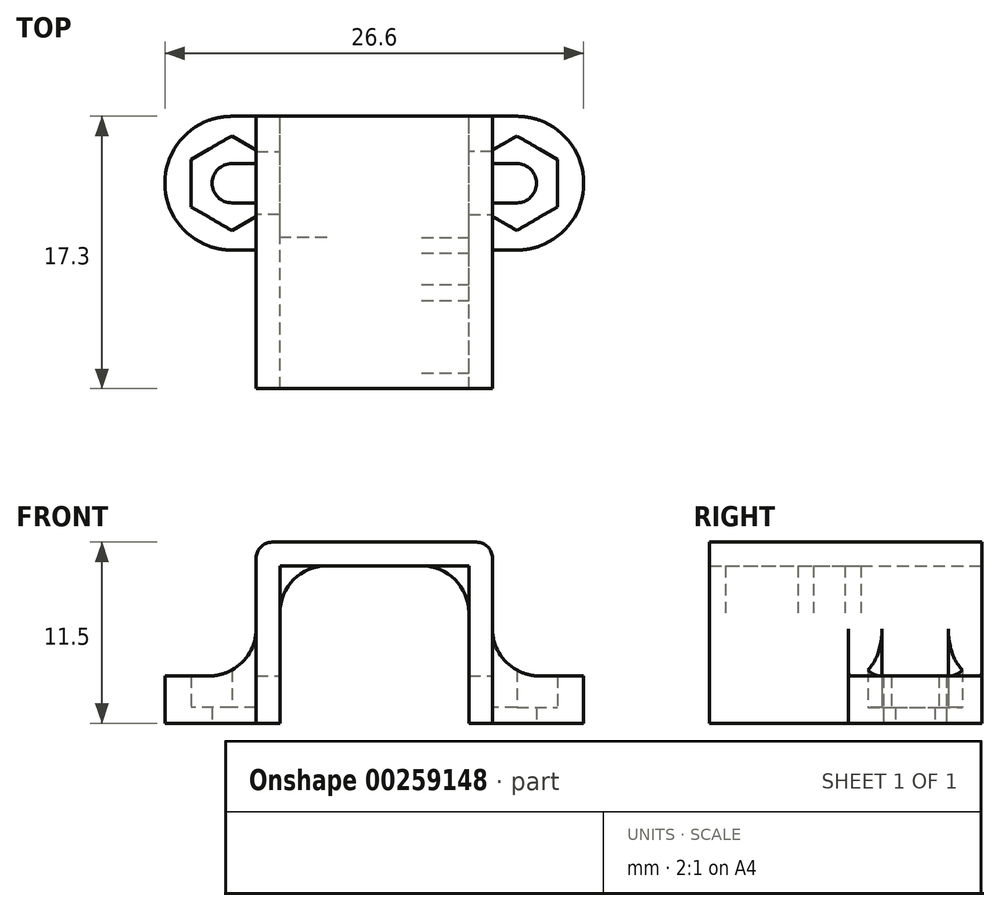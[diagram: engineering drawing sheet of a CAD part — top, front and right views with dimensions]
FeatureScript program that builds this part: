
annotation { "Feature Type Name" : "Feature", "Feature Type Description" : "" }
export const myFeature = defineFeature(function(context is Context, id is Id, definition is map)
    precondition{}
    {
        {
            var Q0;
            Q0=qCreatedBy(makeId("Front.planeOp"),FACE);
            var sketch = newSketch(context, id + "F0", { "sketchPlane" : qUnion([Q0])});
            skLineSegment(sketch, "E0", {"start": v(0, 11.5) * mm, "end": v(-6.5, 11.5) * mm});
            skLineSegment(sketch, "E1", {"start": v(-7.5, 10.5) * mm, "end": v(-7.5, 6) * mm});
            skLineSegment(sketch, "E2", {"start": v(-10.5, 3) * mm, "end": v(-13.3, 3) * mm});
            skLineSegment(sketch, "E3", {"start": v(-13.3, 3) * mm, "end": v(-13.3, 0) * mm});
            skLineSegment(sketch, "E4", {"start": v(-13.3, 0) * mm, "end": v(-6, 0) * mm});
            skLineSegment(sketch, "E5", {"start": v(-6, 0) * mm, "end": v(-6, 7) * mm});
            skLineSegment(sketch, "E6", {"start": v(-3, 10) * mm, "end": v(0, 10) * mm});
            skPoint(sketch, "E7.visualSharp", {"position": v(-7.5, 11.5) * mm});
            skArc(sketch, "E7.filletArc", {"start": v(-6.5, 11.5) * mm, "mid": v(-7.2, 11.2) * mm, "end": v(-7.5, 10.5) * mm});
            skPoint(sketch, "E8.visualSharp", {"position": v(-6, 10) * mm});
            skArc(sketch, "E8.filletArc", {"start": v(-3, 10) * mm, "mid": v(-5.12, 9.12) * mm, "end": v(-6, 7) * mm});
            skPoint(sketch, "E9.visualSharp", {"position": v(-7.5, 3) * mm});
            skArc(sketch, "E9.filletArc", {"start": v(-10.5, 3) * mm, "mid": v(-8.38, 3.88) * mm, "end": v(-7.5, 6) * mm});
            skLineSegment(sketch, "E10.MirrorCS", {"start": v(3, 10) * mm, "end": v(0, 10) * mm});
            skLineSegment(sketch, "E11.MirrorCS", {"start": v(0, 11.5) * mm, "end": v(6.5, 11.5) * mm});
            skArc(sketch, "E12.MirrorCS", {"start": v(3, 10) * mm, "mid": v(5.12, 9.12) * mm, "end": v(6, 7) * mm});
            skArc(sketch, "E13.MirrorCS", {"start": v(6.5, 11.5) * mm, "mid": v(7.2, 11.2) * mm, "end": v(7.5, 10.5) * mm});
            skLineSegment(sketch, "E14.MirrorCS", {"start": v(7.5, 10.5) * mm, "end": v(7.5, 6) * mm});
            skLineSegment(sketch, "E15.MirrorCS", {"start": v(6, 0) * mm, "end": v(6, 7) * mm});
            skArc(sketch, "E16.MirrorCS", {"start": v(10.5, 3) * mm, "mid": v(8.38, 3.88) * mm, "end": v(7.5, 6) * mm});
            skLineSegment(sketch, "E17.MirrorCS", {"start": v(10.5, 3) * mm, "end": v(13.3, 3) * mm});
            skLineSegment(sketch, "E18.MirrorCS", {"start": v(13.3, 3) * mm, "end": v(13.3, 0) * mm});
            skLineSegment(sketch, "E19.MirrorCS", {"start": v(13.3, 0) * mm, "end": v(6, 0) * mm});
            skSolve(sketch);
        }
        {
            var Q0;
            Q0 = qSketchRegion(id + "F0", true);
            extrude(context, id + "F1", {"entities" : qUnion([Q0]), "depth" : 17.3 * mm});
        }
        {
            var Q0;
            Q0=makeQuery(id+"F1.opExtrude","SWEPT_FACE",FACE,{"disambiguationData":[OSD([sQuery(id+"F0.wireOp",EDGE,"E0"),sQuery(id+"F0.wireOp",EDGE,"E11.MirrorCS")])]});
            var sketch = newSketch(context, id + "F2", { "sketchPlane" : qUnion([Q0])});
            skLineSegment(sketch, "E20.2", {"start": v(-6.5, 0) * mm, "end": v(-7.5, 0) * mm});
            skLineSegment(sketch, "E20.3", {"start": v(-6.5, 0) * mm, "end": v(6.5, 0) * mm});
            skLineSegment(sketch, "E20.4", {"start": v(6.5, 0) * mm, "end": v(7.5, 0) * mm});
            skLineSegment(sketch, "E20.7", {"start": v(6.5, -17.3) * mm, "end": v(7.5, -17.3) * mm});
            skLineSegment(sketch, "E20.8", {"start": v(-6.5, -17.3) * mm, "end": v(6.5, -17.3) * mm});
            skLineSegment(sketch, "E20.9", {"start": v(-6.5, -17.3) * mm, "end": v(-7.5, -17.3) * mm});
            skLineSegment(sketch, "E21", {"start": v(-13.3, -4.25) * mm, "end": v(-13.3, -4.25) * mm});
            skLineSegment(sketch, "E22", {"start": v(-9.05, -8.5) * mm, "end": v(-7.5, -8.5) * mm});
            skLineSegment(sketch, "E23", {"start": v(-7.5, -8.5) * mm, "end": v(-7.5, -17.3) * mm});
            skLineSegment(sketch, "E24", {"start": v(7.5, -17.3) * mm, "end": v(7.5, -8.5) * mm});
            skLineSegment(sketch, "E25", {"start": v(7.5, -8.5) * mm, "end": v(9.05, -8.5) * mm});
            skLineSegment(sketch, "E26", {"start": v(13.3, -4.25) * mm, "end": v(13.3, -4.25) * mm});
            skLineSegment(sketch, "E27", {"start": v(-9.05, 0) * mm, "end": v(-7.5, 0) * mm});
            skLineSegment(sketch, "E28", {"start": v(7.5, 0) * mm, "end": v(9.05, 0) * mm});
            skPoint(sketch, "E29.visualSharp", {"position": v(-13.3, 0) * mm});
            skArc(sketch, "E29.filletArc", {"start": v(-9.05, 0) * mm, "mid": v(-12.06, -1.24) * mm, "end": v(-13.3, -4.25) * mm});
            skPoint(sketch, "E30.visualSharp", {"position": v(-13.3, -8.5) * mm});
            skArc(sketch, "E30.filletArc", {"start": v(-13.3, -4.25) * mm, "mid": v(-12.06, -7.26) * mm, "end": v(-9.05, -8.5) * mm});
            skPoint(sketch, "E31.visualSharp", {"position": v(13.3, 0) * mm});
            skArc(sketch, "E31.filletArc", {"start": v(13.3, -4.25) * mm, "mid": v(12.06, -1.24) * mm, "end": v(9.05, 0) * mm});
            skPoint(sketch, "E32.visualSharp", {"position": v(13.3, -8.5) * mm});
            skArc(sketch, "E32.filletArc", {"start": v(9.05, -8.5) * mm, "mid": v(12.06, -7.26) * mm, "end": v(13.3, -4.25) * mm});
            skSolve(sketch);
        }
        {
            var Q0;
            Q0 = qSketchRegion(id + "F2", true);
            extrude(context, id + "F3", {"entities" : qUnion([Q0]), "operationType" : NewBodyOperationType.INTERSECT, "endBound" : BoundingType.THROUGH_ALL, "oppositeDirection" : true, "depth" : 25 * mm});
        }
        {
            var Q0;
            Q0=makeQuery(id+"F1.opExtrude","SWEPT_FACE",FACE,{"disambiguationData":[OSD([sQuery(id+"F0.wireOp",EDGE,"E4")])]});
            var sketch = newSketch(context, id + "F4", { "sketchPlane" : qUnion([Q0])});
            skLineSegment(sketch, "E33", {"start": v(-7.5, 5.5) * mm, "end": v(-9.05, 5.5) * mm});
            skArc(sketch, "E34", {"start": v(-9.05, 5.5) * mm, "mid": v(-10.3, 4.25) * mm, "end": v(-9.05, 3) * mm});
            skLineSegment(sketch, "E35", {"start": v(-9.05, 3) * mm, "end": v(-7.5, 3) * mm});
            skLineSegment(sketch, "E36", {"start": v(-6, 6.25) * mm, "end": v(-7.5, 6.25) * mm});
            skLineSegment(sketch, "E37", {"start": v(-7.5, 6.25) * mm, "end": v(-7.5, 5.5) * mm});
            skLineSegment(sketch, "E38", {"start": v(-7.5, 3) * mm, "end": v(-7.5, 2.25) * mm});
            skLineSegment(sketch, "E39", {"start": v(-7.5, 2.25) * mm, "end": v(-6, 2.25) * mm});
            skLineSegment(sketch, "E40", {"start": v(-6, 6.25) * mm, "end": v(-6, 2.25) * mm});
            skLineSegment(sketch, "E41", {"start": v(4.75, 4.25) * mm, "end": v(-15.15, 4.25) * mm, "construction": true});
            skPoint(sketch, "E41.endSnap0", {"position": v(-10.3, 4.25) * mm});
            skLineSegment(sketch, "E42.MirrorCS", {"start": v(6, 6.25) * mm, "end": v(7.5, 6.25) * mm});
            skLineSegment(sketch, "E43.MirrorCS", {"start": v(6, 6.25) * mm, "end": v(6, 2.25) * mm});
            skLineSegment(sketch, "E44.MirrorCS", {"start": v(7.5, 2.25) * mm, "end": v(6, 2.25) * mm});
            skLineSegment(sketch, "E45.MirrorCS", {"start": v(7.5, 3) * mm, "end": v(7.5, 2.25) * mm});
            skLineSegment(sketch, "E46.MirrorCS", {"start": v(9.05, 3) * mm, "end": v(7.5, 3) * mm});
            skLineSegment(sketch, "E47.MirrorCS", {"start": v(7.5, 5.5) * mm, "end": v(9.05, 5.5) * mm});
            skLineSegment(sketch, "E48.MirrorCS", {"start": v(7.5, 6.25) * mm, "end": v(7.5, 5.5) * mm});
            skArc(sketch, "E49.MirrorCS", {"start": v(9.05, 5.5) * mm, "mid": v(10.3, 4.25) * mm, "end": v(9.05, 3) * mm});
            skSolve(sketch);
        }
        {
            var Q0;
            Q0 = qSketchRegion(id + "F4", true);
            extrude(context, id + "F5", {"entities" : qUnion([Q0]), "operationType" : NewBodyOperationType.REMOVE, "oppositeDirection" : true, "depth" : 3 * mm});
        }
        {
            var Q0;
            Q0=qCreatedBy(makeId("Top.planeOp"),FACE);
            cPlane(context, id + "F6", {"entities" : qUnion([Q0]), "cplaneType" : CPlaneType.OFFSET, "offset" : 1 * mm, "width" : 150 * mm, "height" : 150 * mm});
        }
        {
            var Q0;
            Q0=qCreatedBy(id+"F6.planeOp",FACE);
            var sketch = newSketch(context, id + "F7", { "sketchPlane" : qUnion([Q0])});
            skCircle(sketch, "E50.cCircle", {"center": v(-9.05, -4.25) * mm, "radius": 2.6 * mm, "construction": true});
            skLineSegment(sketch, "E50.0", {"start": v(-11.65, -5.75) * mm, "end": v(-11.65, -2.75) * mm});
            skLineSegment(sketch, "E50.1", {"start": v(-11.65, -2.75) * mm, "end": v(-9.05, -1.25) * mm});
            skLineSegment(sketch, "E50.2", {"start": v(-9.05, -1.25) * mm, "end": v(-7.5, -2.14) * mm});
            skLineSegment(sketch, "E50.4", {"start": v(-7.5, -6.36) * mm, "end": v(-9.05, -7.25) * mm});
            skLineSegment(sketch, "E50.5", {"start": v(-9.05, -7.25) * mm, "end": v(-11.65, -5.75) * mm});
            skPoint(sketch, "E50.0.midPoint", {"position": v(-11.65, -4.25) * mm});
            skPoint(sketch, "E51", {"position": v(-7.5, -6.36) * mm});
            skPoint(sketch, "E52", {"position": v(-7.5, -2.14) * mm});
            skLineSegment(sketch, "E53", {"start": v(-7.5, -6.36) * mm, "end": v(-7.5, -2.14) * mm});
            skLineSegment(sketch, "E54.MirrorCS", {"start": v(7.5, -6.36) * mm, "end": v(9.05, -7.25) * mm});
            skLineSegment(sketch, "E55.MirrorCS", {"start": v(9.05, -7.25) * mm, "end": v(11.65, -5.75) * mm});
            skLineSegment(sketch, "E56.MirrorCS", {"start": v(11.65, -5.75) * mm, "end": v(11.65, -2.75) * mm});
            skLineSegment(sketch, "E57.MirrorCS", {"start": v(11.65, -2.75) * mm, "end": v(9.05, -1.25) * mm});
            skLineSegment(sketch, "E58.MirrorCS", {"start": v(9.05, -1.25) * mm, "end": v(7.5, -2.14) * mm});
            skLineSegment(sketch, "E59.MirrorCS", {"start": v(7.5, -17.3) * mm, "end": v(7.5, 0) * mm, "construction": true});
            skLineSegment(sketch, "E60.MirrorCS", {"start": v(7.5, -6.36) * mm, "end": v(7.5, -2.14) * mm});
            skSolve(sketch);
        }
        {
            var Q0;
            Q0 = qSketchRegion(id + "F7", true);
            extrude(context, id + "F8", {"entities" : qUnion([Q0]), "operationType" : NewBodyOperationType.REMOVE, "endBound" : BoundingType.THROUGH_ALL, "depth" : 25 * mm});
        }
        {
            var Q0;
            Q0=makeQuery(id+"F1.opExtrude","SWEPT_FACE",FACE,{"disambiguationData":[OSD([sQuery(id+"F0.wireOp",EDGE,"E19.MirrorCS")])]});
            var sketch = newSketch(context, id + "F9", { "sketchPlane" : qUnion([Q0])});
            skLineSegment(sketch, "E61.0", {"start": v(3, 17.3) * mm, "end": v(-3, 17.3) * mm, "construction": true});
            skLineSegment(sketch, "E61.1", {"start": v(-6, 17.3) * mm, "end": v(-6, 6.25) * mm, "construction": true});
            skLineSegment(sketch, "E62.bottom", {"start": v(-3, 17.3) * mm, "end": v(-6, 17.3) * mm});
            skLineSegment(sketch, "E62.top", {"start": v(-3, 7.7) * mm, "end": v(-6, 7.7) * mm});
            skLineSegment(sketch, "E62.left", {"start": v(-3, 17.3) * mm, "end": v(-3, 7.7) * mm});
            skLineSegment(sketch, "E62.right", {"start": v(-6, 17.3) * mm, "end": v(-6, 7.7) * mm});
            skLineSegment(sketch, "E63.0", {"start": v(3, 17.3) * mm, "end": v(3, 0) * mm, "construction": true});
            skLineSegment(sketch, "E63.1", {"start": v(6, 17.3) * mm, "end": v(6, 6.25) * mm, "construction": true});
            skLineSegment(sketch, "E64.bottom", {"start": v(3, 17.3) * mm, "end": v(6, 17.3) * mm});
            skLineSegment(sketch, "E64.top", {"start": v(3, 16.3) * mm, "end": v(6, 16.3) * mm});
            skLineSegment(sketch, "E64.left", {"start": v(3, 17.3) * mm, "end": v(3, 16.3) * mm});
            skLineSegment(sketch, "E64.right", {"start": v(6, 17.3) * mm, "end": v(6, 16.3) * mm});
            skLineSegment(sketch, "E65.bottom", {"start": v(3, 7.7) * mm, "end": v(6, 7.7) * mm});
            skLineSegment(sketch, "E65.top", {"start": v(3, 8.7) * mm, "end": v(6, 8.7) * mm});
            skLineSegment(sketch, "E65.left", {"start": v(3, 7.7) * mm, "end": v(3, 8.7) * mm});
            skLineSegment(sketch, "E65.right", {"start": v(6, 7.7) * mm, "end": v(6, 8.7) * mm});
            skLineSegment(sketch, "E66.bottom", {"start": v(3, 11.7) * mm, "end": v(6, 11.7) * mm});
            skLineSegment(sketch, "E66.top", {"start": v(3, 10.7) * mm, "end": v(6, 10.7) * mm});
            skLineSegment(sketch, "E66.left", {"start": v(3, 11.7) * mm, "end": v(3, 10.7) * mm});
            skLineSegment(sketch, "E66.right", {"start": v(6, 11.7) * mm, "end": v(6, 10.7) * mm});
            skSolve(sketch);
        }
        {
            var Q0;
            Q0 = qSketchRegion(id + "F9", true);
            var Q1;
            Q1=makeQuery(id+"F1.opExtrude","SWEPT_FACE",FACE,{"disambiguationData":[OSD([sQuery(id+"F0.wireOp",EDGE,"E6"),sQuery(id+"F0.wireOp",EDGE,"E10.MirrorCS")])]});
            extrude(context, id + "F10", {"entities" : qUnion([Q0]), "operationType" : NewBodyOperationType.REMOVE, "endBound" : BoundingType.UP_TO_SURFACE, "oppositeDirection" : true, "endBoundEntityFace" : qUnion([Q1]), "depth" : 25 * mm});
        }
    });
